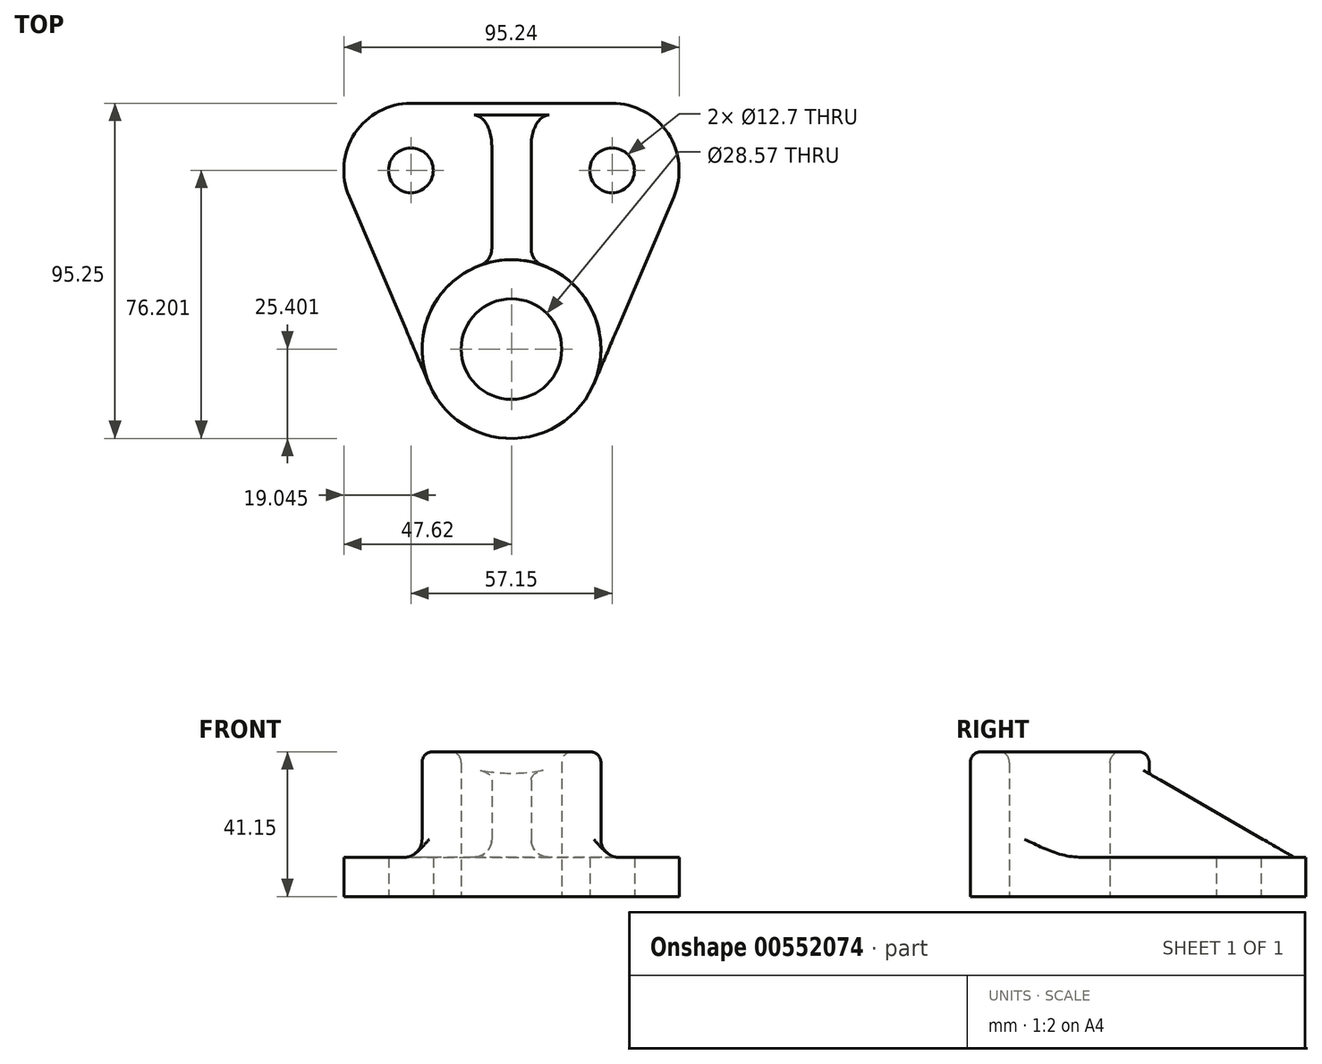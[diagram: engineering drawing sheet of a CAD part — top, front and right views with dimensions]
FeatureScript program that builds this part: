
annotation { "Feature Type Name" : "Feature", "Feature Type Description" : "" }
export const myFeature = defineFeature(function(context is Context, id is Id, definition is map)
    precondition{}
    {
        {
            var Q0;
            Q0=qCreatedBy(makeId("Top.planeOp"),FACE);
            var sketch = newSketch(context, id + "F0", { "sketchPlane" : qUnion([Q0])});
            skCircle(sketch, "E0", {"center": v(0, -35.9) * mm, "radius": 25.4 * mm});
            skLineSegment(sketch, "E1", {"start": v(0, -35.9) * mm, "end": v(0, 33.94) * mm, "construction": true});
            skLineSegment(sketch, "E2", {"start": v(-23.36, -45.88) * mm, "end": v(-46.1, 7.42) * mm});
            skArc(sketch, "E3.filletArc", {"start": v(-28.57, 33.94) * mm, "mid": v(-44.47, 25.4) * mm, "end": v(-46.1, 7.42) * mm});
            skCircle(sketch, "E4", {"center": v(0, -35.9) * mm, "radius": 14.29 * mm});
            skCircle(sketch, "E5", {"center": v(-28.57, 14.9) * mm, "radius": 6.35 * mm});
            skArc(sketch, "E6.0.MirrorCS", {"start": v(28.58, 33.94) * mm, "mid": v(44.47, 25.4) * mm, "end": v(46.1, 7.42) * mm});
            skLineSegment(sketch, "E7.0.MirrorCS", {"start": v(23.36, -45.88) * mm, "end": v(46.1, 7.42) * mm});
            skCircle(sketch, "E8.0.MirrorC", {"center": v(28.58, 14.9) * mm, "radius": 6.35 * mm});
            skLineSegment(sketch, "E9", {"start": v(-28.57, 33.94) * mm, "end": v(28.58, 33.94) * mm});
            skSolve(sketch);
        }
        {
            var Q0;
            Q0=qCreatedBy(makeId("Right.planeOp"),FACE);
            var sketch = newSketch(context, id + "F1", { "sketchPlane" : qUnion([Q0])});
            skLineSegment(sketch, "E10", {"start": v(-61.3, 11.15) * mm, "end": v(-61.3, 52.3) * mm});
            skLineSegment(sketch, "E11", {"start": v(-10.64, 41.94) * mm, "end": v(-10.64, 11.15) * mm});
            skLineSegment(sketch, "E12.0", {"start": v(-13.81, 41.94) * mm, "end": v(-13.81, 11.15) * mm});
            skLineSegment(sketch, "E13", {"start": v(-13.81, 36.81) * mm, "end": v(30.64, 11.15) * mm});
            skLineSegment(sketch, "E14", {"start": v(30.64, 11.15) * mm, "end": v(-13.81, 11.15) * mm});
            skLineSegment(sketch, "E15", {"start": v(-13.81, 11.15) * mm, "end": v(-13.81, 36.81) * mm});
            skSolve(sketch);
        }
        {
            var Q0;
            Q0=makeQuery(id+"F0.imprint","IMPRINT",FACE,{"disambiguationData":[TD([[makeQuery(id+"F0.imprint","IMPRINT",EDGE,{"derivedFrom":sQuery(id+"F0.wireOp",EDGE,"E4")}),-1.0]])]});
            extrude(context, id + "F2", {"entities" : qUnion([Q0]), "depth" : 41.15 * mm, "offsetDistance" : 25.4 * mm});
        }
        {
            var Q0;
            Q0 = qSketchRegion(id + "F0", true);
            extrude(context, id + "F3", {"entities" : qUnion([Q0]), "operationType" : NewBodyOperationType.ADD, "depth" : 11.18 * mm, "offsetDistance" : 25.4 * mm});
        }
        {
            var Q0;
            {var subQ0=sQuery(id+"F1.wireOp",EDGE,"E14");var subQ1=sQuery(id+"F1.wireOp",EDGE,"E11");var subQ2=makeQuery(id+"F1.imprint","INTERSECT",VERTEX,{"derivedFrom":[subQ1,subQ0]});Q0=makeQuery(id+"F1.imprint","IMPRINT",FACE,{"disambiguationData":[TD([[makeQuery(id+"F1.imprint","IMPRINT",EDGE,{"disambiguationData":[TD([[subQ2,1.0]])],"derivedFrom":subQ1}),1.0]])]});}
            var Q1;
            Q1 = qSketchRegion(id + "F1", true);
            extrude(context, id + "F4", {"entities" : qUnion([Q0, Q1]), "operationType" : NewBodyOperationType.ADD, "endBound" : BoundingType.SYMMETRIC, "depth" : 11.18 * mm, "offsetDistance" : 25.4 * mm});
        }
        {
            var Q0;
            Q0=makeQuery(id+"F4.boolean.opBoolean","INTERSECT",EDGE,{"derivedFrom":[makeQuery(id+"F2.opExtrude","SWEPT_FACE",FACE,{"disambiguationData":[OSD([sQuery(id+"F0.wireOp",EDGE,"E0")])]}),makeQuery(id+"F4.opExtrude","CAP_FACE",FACE,{"disambiguationData":[OSD([sQuery(id+"F1.wireOp",EDGE,"E13"),sQuery(id+"F1.wireOp",EDGE,"E14"),sQuery(id+"F1.wireOp",EDGE,"E15")])],"isStart":false})]});
            var Q1;
            Q1=makeQuery(id+"F4.boolean.opBoolean","INTERSECT",EDGE,{"derivedFrom":[makeQuery(id+"F3.opExtrude","CAP_FACE",FACE,{"disambiguationData":[OSD([sQuery(id+"F0.wireOp",EDGE,"E0"),sQuery(id+"F0.wireOp",EDGE,"E2"),sQuery(id+"F0.wireOp",EDGE,"E3.filletArc"),sQuery(id+"F0.wireOp",EDGE,"E4"),sQuery(id+"F0.wireOp",EDGE,"E5"),sQuery(id+"F0.wireOp",EDGE,"E6.0.MirrorCS"),sQuery(id+"F0.wireOp",EDGE,"E7.0.MirrorCS"),sQuery(id+"F0.wireOp",EDGE,"E8.0.MirrorC"),sQuery(id+"F0.wireOp",EDGE,"E9")])],"isStart":false}),makeQuery(id+"F4.opExtrude","CAP_FACE",FACE,{"disambiguationData":[OSD([sQuery(id+"F1.wireOp",EDGE,"E13"),sQuery(id+"F1.wireOp",EDGE,"E14"),sQuery(id+"F1.wireOp",EDGE,"E15")])],"isStart":false})]});
            var Q2;
            Q2=makeQuery(id+"F4.boolean.opBoolean","INTERSECT",EDGE,{"derivedFrom":[makeQuery(id+"F2.opExtrude","SWEPT_FACE",FACE,{"disambiguationData":[OSD([sQuery(id+"F0.wireOp",EDGE,"E0")])]}),makeQuery(id+"F4.opExtrude","CAP_FACE",FACE,{"disambiguationData":[OSD([sQuery(id+"F1.wireOp",EDGE,"E13"),sQuery(id+"F1.wireOp",EDGE,"E14"),sQuery(id+"F1.wireOp",EDGE,"E15")])],"isStart":true})]});
            var Q3;
            Q3=makeQuery(id+"F4.boolean.opBoolean","INTERSECT",EDGE,{"derivedFrom":[makeQuery(id+"F3.opExtrude","CAP_FACE",FACE,{"disambiguationData":[OSD([sQuery(id+"F0.wireOp",EDGE,"E0"),sQuery(id+"F0.wireOp",EDGE,"E2"),sQuery(id+"F0.wireOp",EDGE,"E3.filletArc"),sQuery(id+"F0.wireOp",EDGE,"E4"),sQuery(id+"F0.wireOp",EDGE,"E5"),sQuery(id+"F0.wireOp",EDGE,"E6.0.MirrorCS"),sQuery(id+"F0.wireOp",EDGE,"E7.0.MirrorCS"),sQuery(id+"F0.wireOp",EDGE,"E8.0.MirrorC"),sQuery(id+"F0.wireOp",EDGE,"E9")])],"isStart":false}),makeQuery(id+"F4.opExtrude","CAP_FACE",FACE,{"disambiguationData":[OSD([sQuery(id+"F1.wireOp",EDGE,"E13"),sQuery(id+"F1.wireOp",EDGE,"E14"),sQuery(id+"F1.wireOp",EDGE,"E15")])],"isStart":true})]});
            var Q4;
            {var subQ0=sQuery(id+"F0.wireOp",EDGE,"E0");var subQ1=makeQuery(id+"F2.opExtrude","SWEPT_FACE",FACE,{"disambiguationData":[OSD([subQ0])]});var subQ2=sQuery(id+"F0.wireOp",EDGE,"E7.0.MirrorCS");var subQ3=makeQuery(id+"F3.opExtrude","CAP_FACE",FACE,{"disambiguationData":[OSD([subQ0,sQuery(id+"F0.wireOp",EDGE,"E2"),sQuery(id+"F0.wireOp",EDGE,"E3.filletArc"),sQuery(id+"F0.wireOp",EDGE,"E4"),sQuery(id+"F0.wireOp",EDGE,"E5"),sQuery(id+"F0.wireOp",EDGE,"E6.0.MirrorCS"),subQ2,sQuery(id+"F0.wireOp",EDGE,"E8.0.MirrorC"),sQuery(id+"F0.wireOp",EDGE,"E9")])],"isStart":false});Q4=makeQuery(id+"F4.boolean.opBoolean","SPLIT",EDGE,{"disambiguationData":[TD([makeQuery(id+"F3.opExtrude","SWEPT_FACE",FACE,{"disambiguationData":[OSD([subQ2])]})])],"derivedFrom":makeQuery(id+"F3.boolean.opBoolean","INTERSECT",EDGE,{"derivedFrom":[subQ1,subQ3]})});}
            var Q5;
            {var subQ0=sQuery(id+"F0.wireOp",EDGE,"E0");var subQ1=makeQuery(id+"F2.opExtrude","SWEPT_FACE",FACE,{"disambiguationData":[OSD([subQ0])]});var subQ2=sQuery(id+"F0.wireOp",EDGE,"E2");var subQ3=makeQuery(id+"F3.opExtrude","CAP_FACE",FACE,{"disambiguationData":[OSD([subQ0,subQ2,sQuery(id+"F0.wireOp",EDGE,"E3.filletArc"),sQuery(id+"F0.wireOp",EDGE,"E4"),sQuery(id+"F0.wireOp",EDGE,"E5"),sQuery(id+"F0.wireOp",EDGE,"E6.0.MirrorCS"),sQuery(id+"F0.wireOp",EDGE,"E7.0.MirrorCS"),sQuery(id+"F0.wireOp",EDGE,"E8.0.MirrorC"),sQuery(id+"F0.wireOp",EDGE,"E9")])],"isStart":false});Q5=makeQuery(id+"F4.boolean.opBoolean","SPLIT",EDGE,{"disambiguationData":[TD([makeQuery(id+"F3.opExtrude","SWEPT_FACE",FACE,{"disambiguationData":[OSD([subQ2])]})])],"derivedFrom":makeQuery(id+"F3.boolean.opBoolean","INTERSECT",EDGE,{"derivedFrom":[subQ1,subQ3]})});}
            fillet(context, id + "F5", {"entities" : qUnion([Q0, Q1, Q2, Q3, Q4, Q5]), "radius" : 5.08 * mm, "tangentPropagation" : true, "allowEdgeOverflow" : false});
        }
        {
            var Q0;
            Q0=makeQuery(id+"F2.opExtrude","CAP_FACE",FACE,{"disambiguationData":[OSD([sQuery(id+"F0.wireOp",EDGE,"E0"),sQuery(id+"F0.wireOp",EDGE,"E4")])],"isStart":false});
            fillet(context, id + "F6", {"entities" : qUnion([Q0]), "radius" : 3.05 * mm, "tangentPropagation" : true, "allowEdgeOverflow" : false});
        }
    });
